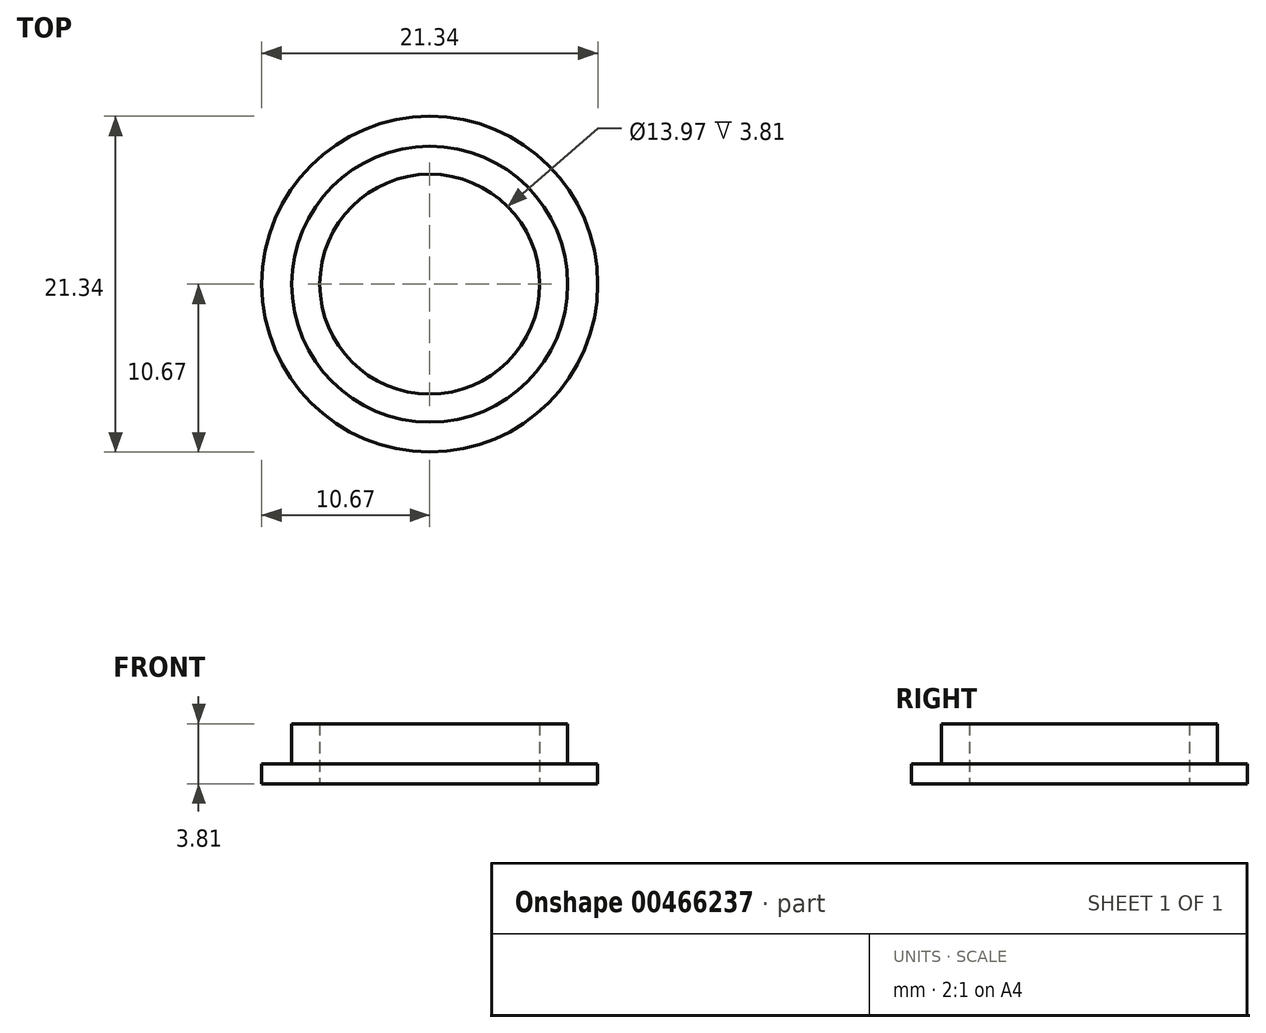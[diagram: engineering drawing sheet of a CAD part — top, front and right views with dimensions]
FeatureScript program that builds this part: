
annotation { "Feature Type Name" : "Feature", "Feature Type Description" : "" }
export const myFeature = defineFeature(function(context is Context, id is Id, definition is map)
    precondition{}
    {
        {
            var Q0;
            Q0=qCreatedBy(makeId("Right.planeOp"),FACE);
            var sketch = newSketch(context, id + "F0", { "sketchPlane" : qUnion([Q0])});
            skLineSegment(sketch, "E0", {"start": v(0, 0) * mm, "end": v(0, 15) * mm, "construction": true});
            skLineSegment(sketch, "E1", {"start": v(6.98, 3.81) * mm, "end": v(6.99, 0) * mm});
            skLineSegment(sketch, "E2", {"start": v(6.99, 0) * mm, "end": v(10.67, 0) * mm});
            skLineSegment(sketch, "E3", {"start": v(10.67, 0) * mm, "end": v(10.67, 1.27) * mm});
            skLineSegment(sketch, "E4", {"start": v(10.67, 1.27) * mm, "end": v(8.76, 1.27) * mm});
            skLineSegment(sketch, "E5", {"start": v(8.76, 1.27) * mm, "end": v(8.76, 3.81) * mm});
            skLineSegment(sketch, "E6", {"start": v(8.76, 3.81) * mm, "end": v(6.99, 3.81) * mm});
            skSolve(sketch);
        }
        {
            var Q0;
            Q0=makeQuery(id+"F0.imprint","IMPRINT",FACE,{"disambiguationData":[TD([[makeQuery(id+"F0.imprint","IMPRINT",EDGE,{"derivedFrom":sQuery(id+"F0.wireOp",EDGE,"E1")}),1.0]])]});
            var Q1;
            Q1=sQuery(id+"F0.wireOp",EDGE,"E0");
            revolve(context, id + "F1", {"entities" : qUnion([Q0]), "axis" : qUnion([Q1]), "revolveType" : RevolveType.FULL});
        }
    });
